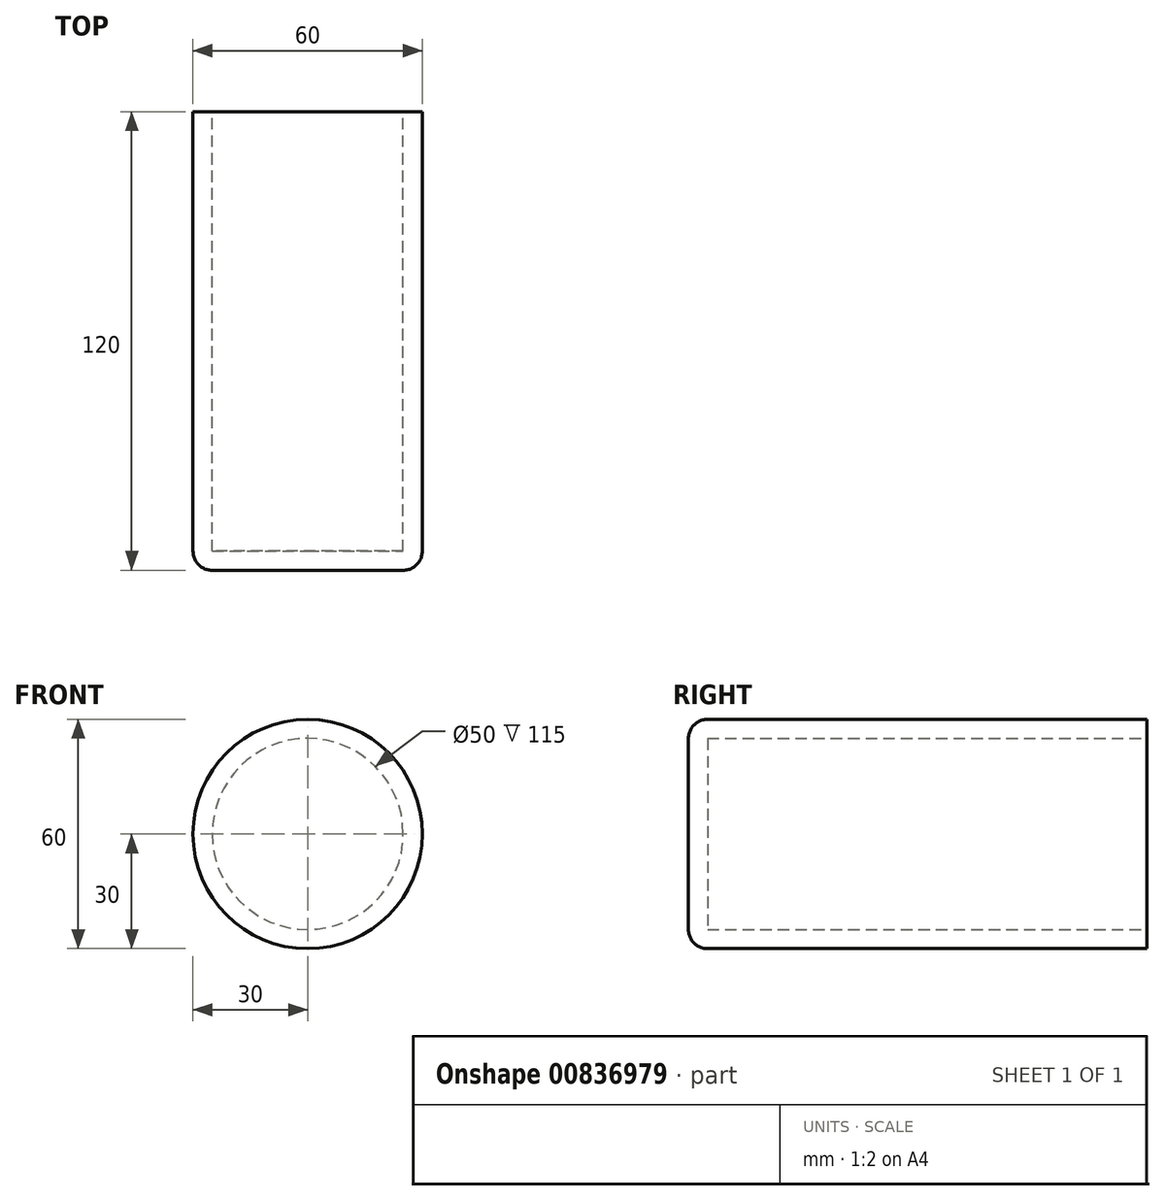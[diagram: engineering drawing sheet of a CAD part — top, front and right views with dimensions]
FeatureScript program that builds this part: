
annotation { "Feature Type Name" : "Feature", "Feature Type Description" : "" }
export const myFeature = defineFeature(function(context is Context, id is Id, definition is map)
    precondition{}
    {
        {
            var Q0;
            Q0=qCreatedBy(makeId("Front.planeOp"),FACE);
            var sketch = newSketch(context, id + "F0", { "sketchPlane" : qUnion([Q0])});
            skCircle(sketch, "E0", {"center": v(0, 0) * mm, "radius": 30 * mm});
            skSolve(sketch);
        }
        {
            var Q0;
            Q0=makeQuery(id+"F0.imprint","IMPRINT",FACE,{"disambiguationData":[TD([[makeQuery(id+"F0.imprint","IMPRINT",EDGE,{"derivedFrom":sQuery(id+"F0.wireOp",EDGE,"E0")}),1.0]])]});
            extrude(context, id + "F1", {"entities" : qUnion([Q0]), "depth" : 120 * mm, "offsetDistance" : 25 * mm});
        }
        {
            var Q0;
            Q0=makeQuery(id+"F1.opExtrude","CAP_FACE",FACE,{"disambiguationData":[OSD([sQuery(id+"F0.wireOp",EDGE,"E0")])],"isStart":true});
            var sketch = newSketch(context, id + "F2", { "sketchPlane" : qUnion([Q0])});
            skCircle(sketch, "E1", {"center": v(0, 0) * mm, "radius": 25 * mm});
            skSolve(sketch);
        }
        {
            var Q0;
            Q0=makeQuery(id+"F2.imprint","IMPRINT",FACE,{"disambiguationData":[TD([[makeQuery(id+"F2.imprint","IMPRINT",EDGE,{"derivedFrom":sQuery(id+"F2.wireOp",EDGE,"E1")}),1.0]])]});
            extrude(context, id + "F3", {"entities" : qUnion([Q0]), "operationType" : NewBodyOperationType.REMOVE, "oppositeDirection" : true, "depth" : 115 * mm, "offsetDistance" : 25 * mm});
        }
        {
            var Q0;
            Q0=makeQuery(id+"F1.opExtrude","CAP_EDGE",EDGE,{"disambiguationData":[OSD([sQuery(id+"F0.wireOp",EDGE,"E0")])],"isStart":false});
            fillet(context, id + "F4", {"entities" : qUnion([Q0]), "radius" : 5 * mm, "tangentPropagation" : true, "allowEdgeOverflow" : false});
        }
    });
